# Revit family: DLC7
name_source: partatom
category: Communication Devices
units: mm (PartAtom-declared; Revit-internal decimal feet)

## family parameters
Cut with Voids When Loaded = No
Host = Face
Maintain Annotation Orientation = No
OmniClass Number = 23.85.80.11.27
OmniClass Title = Lighting Controls
Part Type = Normal
Room Calculation Point = No
Round Connector Dimension = Use Diameter
Shared = Yes

## types (1)
- DLC7
    Assembly Code = D5090
    Black = Paint -  Carbon Black
    Certifications = ETL/UL 916
    Default Elevation = 48 "
    Description = Our DLC7 is the ideal system for providing continuous dimming control for
2-wire 0–10V dimming ballasts based on natural daylight. This control maintains
constant, undisturbed, fluorescent light levels during peak use times. Through
continuous monitoring of ambient light levels, the DLC7 dims the associated
lighting fixtures to a user’s predefined foot-candle setting. The DLC7 dimming
photocell provides precise control of the actual amount of lighting on the work
surface (e.g. desktop, floor) within its field of view. Measured light levels are
converted into a linear, proportional, analog voltage that controls the ballastdimming range. This achieves maximum energy savings by efficiently blending
natural and artificial light to maintain a comfortable visual environment.
    Features = Controls 2-wire 0–10V dimming ballasts
• Light-sensitivity range of 0–500FC
• Selectable 3- or 8-second dimming rate
• Multiple calibration options
• Low-profile design
• Five-year limited warranty
• Low voltage device: 24 Vdc
    Gray = Paint -  Gray Smooth
    Height = 4.5 "
    Manufacturer = NX Lighting Controls
    Model = DLC7
    Mount Type = Ceiling, Surface
    Space Planning = Stand-Alone Solutions
    Type Comments = Daylight Harvesting Controls
    URL = https://www.currentlighting.com
    Warranty = 5-Years Warranty
    Width = 2 "

## geometry (parser evidence)
native form markers: Sweep x3
no freeform markers — native parametric forms only
